# Revit family: 70M23XX30XX
name_source: partatom
category: Furniture
units: mm (PartAtom-declared; Revit-internal decimal feet)

## family parameters
Always vertical = Yes
Cut with Voids When Loaded = No
OmniClass Number = 23.40.20.00
OmniClass Title = General Furniture and Specialties
Room Calculation Point = No
Shared = No
Work Plane-Based = No

## types (4) — shared parameters
Caster = Caster,  Black
Glide = Glide,  Black
Leg Fit-Dist = 27 3/8"
Manufacturer = Palmer Hamilton
Type Comments = Wall Pocket
URL = https://palmerhamilton.com

## per-type parameters (varying)
| type | 12'W Handle | 12-27h | 12-29h | 12L | 14'W Handle | 14-29H | 14L | Depth | Description | Height | L | LH | Leg Dist |
| 70M23273012 | Yes | Yes | No | Yes | No | No | No | 142" | Wall Pocket Table,27"H x 30"W x 12' L | 27" | Yes | No | 23 1/8" |
| 70M23273014 | Yes | Yes | No | No | Yes | No | Yes | 166" | Wall Pocket Table,27"H x 30"W x 14' L | 27" | No | Yes | 23 5/8" |
| 70M23293012 | Yes | No | Yes | Yes | No | No | No | 142" | Wall Pocket Table,29"H x 30"W x 12' L | 29" | Yes | No | 25 7/8" |
| 70M23293014 | No | No | No | No | Yes | Yes | Yes | 166" | Wall Pocket Table,29"H x 30"W x 14' L | 29" | No | Yes | 25 5/8" |

note: column(s) folded — value = type name in every type: Model

## geometry (parser evidence)
native form markers: Sweep x27
no freeform markers — native parametric forms only
